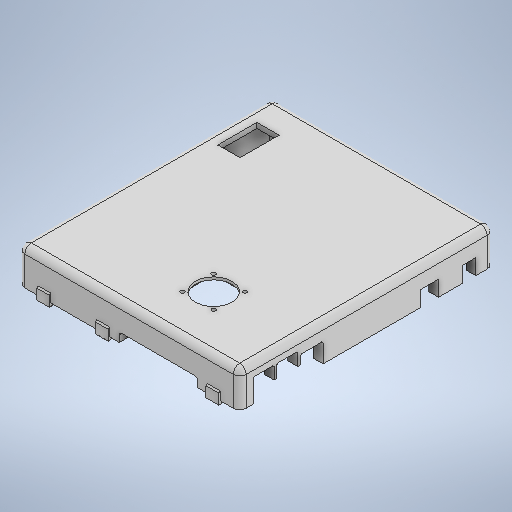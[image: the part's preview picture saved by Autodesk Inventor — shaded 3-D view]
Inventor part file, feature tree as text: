
AUTODESK INVENTOR PART (.ipt)
format: ipt  version: 2025.2 (Build 292293000, 293)  size: 584,704 bytes
history: native  units: mm
features: extrude x20, sketch x8, plane x5, fillet x4, shell x1, chamfer x1, mirror x1
ambient origin geometry x8: Origin, YZ Plane, XZ Plane, XY Plane, X Axis, Y Axis, Z Axis, Center Point
bodies: Solid1 (feature_tree)
feature tree (40):
  extrude  "Extrusion1"  Depth=7.5mm
  shell  "Shell1"  Thickness=155.0mm
  sketch  "Sketch2"  dims[d10=3.0mm d12=21.0mm]
  extrude  "Board Ports"  Depth=21.0mm
  extrude  "Pi Power Suppply"  Depth=163.5mm
  fillet  "Fillet4"  Radius=10.33mm
  extrude  "Extrusion10"  Depth=180.0mm
  extrude  "Pi Ethernet port"  Depth=85.0mm
  chamfer  "Chamfer1"  Distance=18.0mm
  extrude  "Arduino Ports"  Depth=39.0mm
  fillet  "Fillet1"  Radius=0.8mm
  fillet  "Fillet6"  Radius=2.5mm
  plane  "Work Plane6"
  plane  "Work Plane7"
  plane  "Work Plane9"
  sketch  "Sketch3"  dims[d16=131.5mm d18=163.5mm d19=10.33mm]
  extrude  "Snap tab 1"  TaperAngle=45.0deg  [1 undecoded]
  extrude  "Snap tab 1 Groove"  Depth=9.8mm TaperAngle=0.0deg
  extrude  "Snap tab 2"  Depth=9.8mm TaperAngle=0.0deg
  extrude  "Snap tab 2 Groove"  Depth=7.0mm TaperAngle=0.0deg
  extrude  "Snap tab 3"  Depth=8.0mm TaperAngle=0.0deg
  extrude  "Snap tab 3 GRoove"  Depth=15.0mm TaperAngle=0.0deg
  fillet  "Fillet5"  Radius=12.0mm
  plane  "Work Plane11"
  mirror  "Mirror1"
  extrude  "DC terminal port"  [1 undecoded]
  plane  "Work Plane10"
  extrude  "DC terminal fitting"  [1 undecoded]
  sketch  "Sketch7"  dims[d26=5.0mm d29=39.0mm d35=0.8mm d36=2.5mm]
  extrude  "Motor driver heat sink hole"  [1 undecoded]
  extrude  "Base thinning"  TaperAngle=0.0deg  [1 undecoded]
  extrude  "Fan recess face"  Depth=10.0mm
  extrude  "Fan mounting holes"  Depth=2.0mm
  extrude  "Fan opening"  Depth=10.5mm
  extrude  "Extra cable slot"  Depth=14.0mm
  sketch  "Sketch1"  dims[d0=20.0mm d1=0.0mm d2=7.5mm d9=155.0mm]
  sketch  "Sketch4"  dims[d20=13.64mm d21=180.0mm]
  sketch  "Sketch5"  dims[d22=25.0mm d23=85.0mm d24=18.0mm d25=0.0mm]
  sketch  "Sketch8"  dims[d37=1.0mm d38=45.0deg]
  sketch  "Sketch10"  dims[d39=9.8mm d40=0.0mm d43=9.8mm d44=0.0mm d50=9.8mm d51=0.0mm d52=7.0mm d53=0.0mm d54=8.0mm d55=0.0mm d56=15.0mm d57=0.0mm d58=12.0mm d59=0.0mm d60=-20.0mm d61=-105.0mm d63=-150.0mm d65=0.0mm d66=0.0mm d67=10.0mm d68=27.0mm d69=10.5mm d70=14.0mm d71=13.0mm d74=3.0mm d75=0.0mm d83=15.8mm d84=45.8mm d85=4.0mm d86=21.0mm d87=20.0mm d88=0.0mm d89=3.5mm d90=0.0mm d91=30.5mm d92=30.5mm d93=3.0mm d95=24.0mm d96=24.0mm d97=2.0mm d98=0.0mm d99=0.0mm d100=0.0mm d101=28.0mm d102=10.0mm d103=0.0mm d118=50.0mm d119=8.0mm d120=12.0mm d125=10.0mm d126=0.0mm d127=2.0mm d128=45.0deg d129=1.0mm d130=0.6mm d131=4.0mm d132=0.0mm d133=8.0mm d134=4.0mm d135=0.0mm d136=4.0mm d137=0.0mm d142=16.0mm d143=16.0mm d144=17.5mm d145=15.0mm d146=6.0mm d147=1.0mm d148=2.0mm d149=55.0mm d150=35.0mm d151=1.0mm d152=2.0mm d153=45.0deg]
note: 5 required parameter values undecoded (feature->parameter linkage not recoverable at this tier; creation-order binding heuristic only, values carry confidence <= 0.55)
